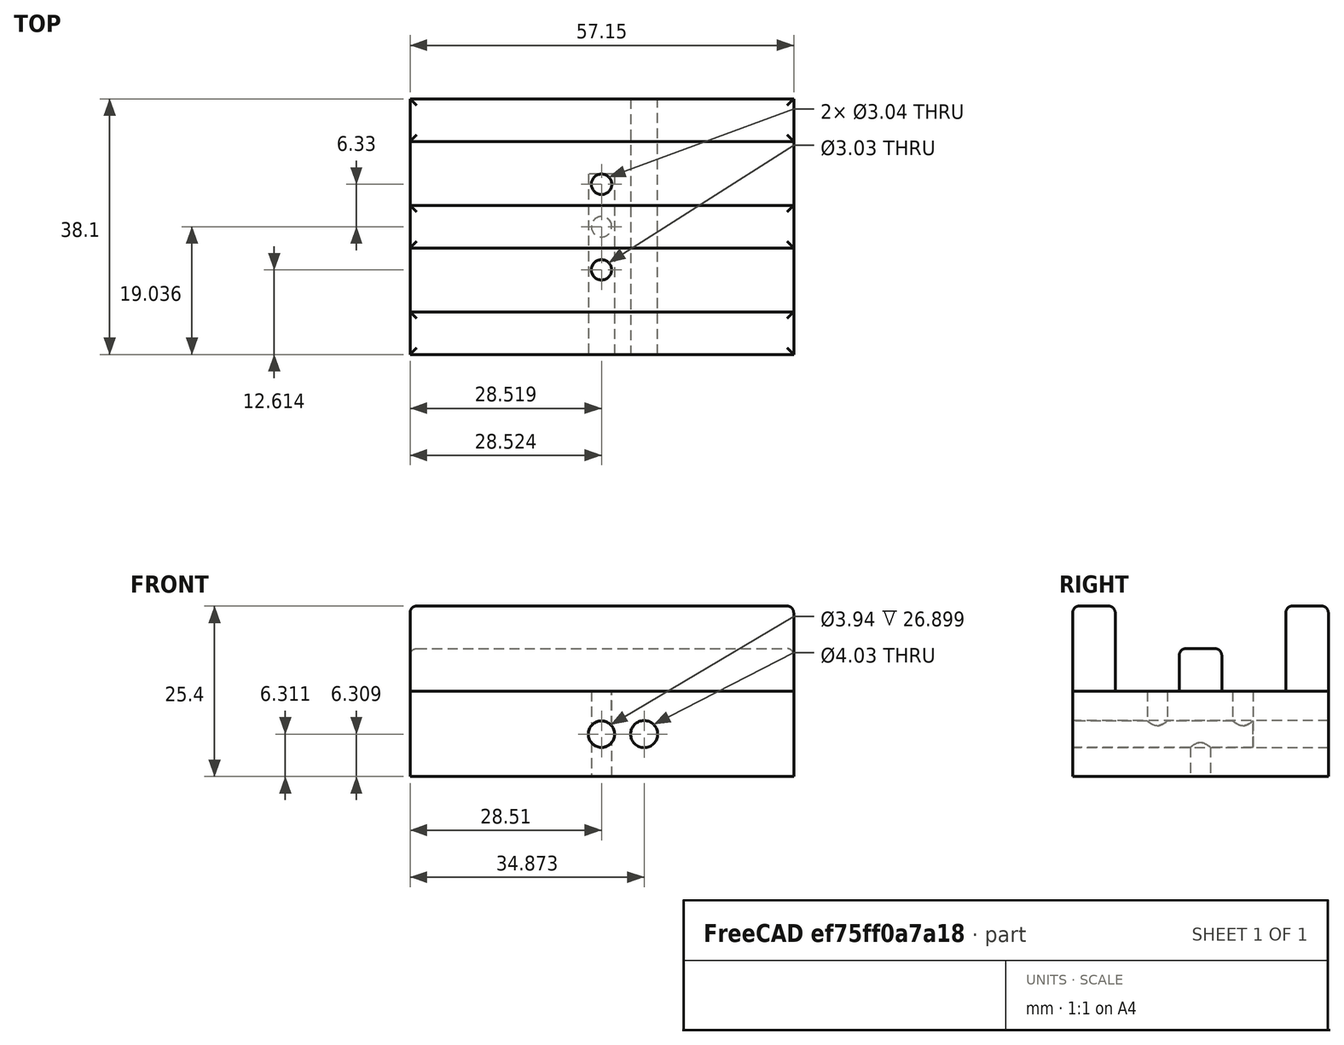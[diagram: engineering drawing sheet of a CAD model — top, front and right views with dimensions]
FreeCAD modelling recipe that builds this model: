
FCSTD DOCUMENT  (FreeCAD 0.15R4671 (Git))
Label: grease_ninja2
License: All rights reserved
LicenseURL: http://en.wikipedia.org/wiki/All_rights_reserved
objects: Sketcher::SketchObject×6, PartDesign::Pad×5, Part::Box×4, Part::Cut×4, Part::Fillet×3, Part::MultiFuse×3
note: 30 computed .brp shape members not serialized (recipe doc carries the construction recipe); baked Part::Feature solids carry a one-line shape summary decoded from their .brp

FEATURE [Part::Box] Box  label="Cube"
  Height = 12.7
  Length = 57.15
  Width = 38.1
FEATURE [Part::Box] Box001  label="Cube001"
  Height = 12.7
  Length = 57.15
  Placement = pos=(0,0,12.7) rot=(0,0,1;0rad)
  Width = 6.35
FEATURE [Part::Box] Box002  label="Cube002"
  Height = 12.7
  Length = 57.15
  Placement = pos=(0,31.75,12.7) rot=(0,0,1;0rad)
  Width = 6.35
FEATURE [Part::Box] Box003  label="Cube003"
  Height = 6.35
  Length = 57.15
  Placement = pos=(0,15.875,12.7) rot=(0,0,1;0rad)
  Width = 6.35
FEATURE [Part::Fillet] Fillet
  Base = -> Box001
  Edges = 4 edges r=1: [Edge2,Edge6,Edge10,Edge12]
FEATURE [Part::Fillet] Fillet001
  Base = -> Box002
  Edges = 4 edges r=1: [Edge2,Edge6,Edge10,Edge12]
FEATURE [Part::Fillet] Fillet002
  Base = -> Box003
  Edges = 4 edges r=1: [Edge2,Edge6,Edge10,Edge12]
FEATURE [Sketcher::SketchObject] Sketch
FEATURE [Sketcher::SketchObject] Sketch001
  sketch-geometry (1):
    g0: Circle CenterX=28.5242 CenterY=19.0362 CenterZ=0 NormalX=0 NormalY=0 NormalZ=1 Radius=1.5192
FEATURE [PartDesign::Pad] Pad
  Length = 6.35
  Length2 = 100
  Sketch = -> Sketch001
  Type = 0
FEATURE [Part::Cut] Cut
  Base = -> Box
  Tool = -> Pad
FEATURE [Sketcher::SketchObject] Sketch002
  Placement = pos=(0,0,0) rot=(1,0,0;1.5708rad)
  sketch-geometry (1):
    g0: Circle CenterX=28.5099 CenterY=6.30875 CenterZ=0 NormalX=0 NormalY=0 NormalZ=1 Radius=1.96842
FEATURE [PartDesign::Pad] Pad001
  Length = 26.8986
  Length2 = 100
  Placement = pos=(0,0,0) rot=(1,0,0;1.5708rad)
  Reversed = true
  Sketch = -> Sketch002
  Type = 0
FEATURE [Sketcher::SketchObject] Sketch003
  Placement = pos=(0,0,6.35) rot=(0,0,1;0rad)
  sketch-geometry (1):
    g0: Circle CenterX=28.5188 CenterY=12.6142 CenterZ=0 NormalX=0 NormalY=0 NormalZ=1 Radius=1.5136
FEATURE [PartDesign::Pad] Pad002
  Length = 6.35
  Length2 = 100
  Placement = pos=(0,0,6.35) rot=(0,0,1;0rad)
  Sketch = -> Sketch003
  Type = 0
FEATURE [Sketcher::SketchObject] Sketch004
  Placement = pos=(0,0,6.35) rot=(0,0,1;0rad)
  sketch-geometry (1):
    g0: Circle CenterX=28.5237 CenterY=25.3664 CenterZ=0 NormalX=0 NormalY=0 NormalZ=1 Radius=1.52075
FEATURE [PartDesign::Pad] Pad003
  Length = 6.35
  Length2 = 100
  Placement = pos=(0,0,6.35) rot=(0,0,1;0rad)
  Sketch = -> Sketch004
  Type = 0
FEATURE [Part::MultiFuse] Fusion
  Shapes = -> [Pad002,Pad001,Pad003]
FEATURE [Part::MultiFuse] Fusion001
  Shapes = -> [Pad,Fusion]
FEATURE [Part::Cut] Cut001
  Base = -> Cut
  Tool = -> Fusion001
FEATURE [Sketcher::SketchObject] Sketch005
  Placement = pos=(0,0,0) rot=(1,0,0;1.5708rad)
  sketch-geometry (1):
    g0: Circle CenterX=34.873 CenterY=6.31109 CenterZ=0 NormalX=0 NormalY=0 NormalZ=1 Radius=2.01665
FEATURE [PartDesign::Pad] Pad004
  Length = 38.1
  Length2 = 100
  Placement = pos=(0,0,0) rot=(1,0,0;1.5708rad)
  Reversed = true
  Sketch = -> Sketch005
  Type = 0
FEATURE [Part::Cut] Cut002
  Base = -> Cut001
  Tool = -> Pad004
FEATURE [Part::MultiFuse] Fusion002
  Shapes = -> [Pad003,Pad001,Pad002,Pad]
FEATURE [Part::Cut] Cut003
  Base = -> Cut002
  Tool = -> Fusion002
